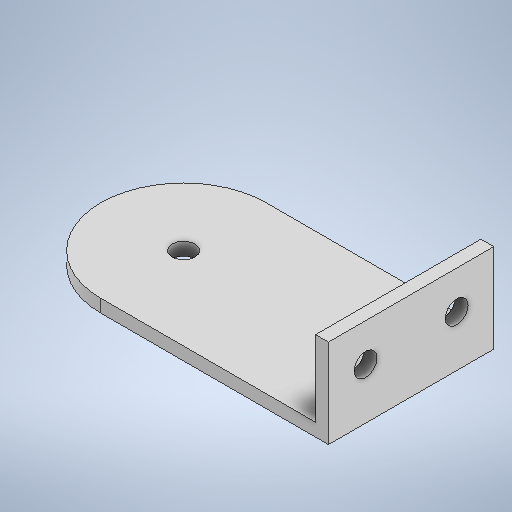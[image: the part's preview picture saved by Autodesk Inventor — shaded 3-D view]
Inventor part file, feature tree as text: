
AUTODESK INVENTOR PART (.ipt)
format: ipt  version: 2025.2 (Build 292293000, 293)  size: 262,144 bytes
history: native  units: in
note: dims shown in document units (in); Inventor stores cm internally (conversion verified against a paired STEP export)
features: extrude x4, sketch x4
ambient origin geometry x8: Origin, YZ Plane, XZ Plane, XY Plane, X Axis, Y Axis, Z Axis, Center Point
bodies: Solid1 (feature_tree)
feature tree (8):
  extrude  "Extrusion1"  Depth=0.4291in
  extrude  "Extrusion2"  Depth=0.8583in
  extrude  "Extrusion3"  Depth=0.0669in
  extrude  "Extrusion4"  Depth=0.0669in
  sketch  "Sketch1"  dims[d2=0.4291in d3=1.1811in]
  sketch  "Sketch2"  dims[d4=1.1811in d5=0.8583in]
  sketch  "Sketch3"  dims[d6=0.0669in d7=0.0in d8=0.1181in]
  sketch  "Sketch4"  dims[d9=0.0669in d10=0.0in d11=0.0669in d12=0.3937in d13=0.0in d14=0.1181in d15=0.1181in d16=0.4724in d17=0.0in d18=0.1969in d19=0.1929in d20=0.3937in d21=0.0in]
